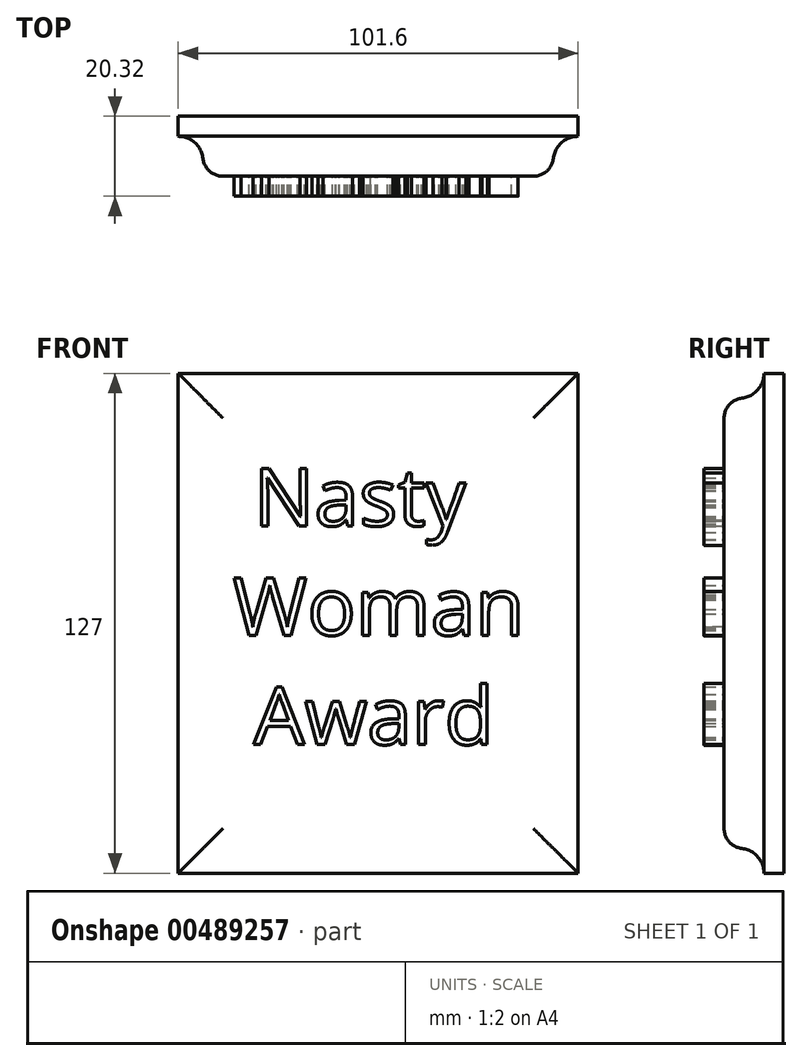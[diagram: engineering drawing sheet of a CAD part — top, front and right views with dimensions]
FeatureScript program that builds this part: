
annotation { "Feature Type Name" : "Feature", "Feature Type Description" : "" }
export const myFeature = defineFeature(function(context is Context, id is Id, definition is map)
    precondition{}
    {
        {
            var Q0;
            Q0=qCreatedBy(makeId("Front.planeOp"),FACE);
            var sketch = newSketch(context, id + "F0", { "sketchPlane" : qUnion([Q0])});
            skLineSegment(sketch, "E0.bottom", {"start": v(-101.6, 127) * mm, "end": v(0, 127) * mm});
            skLineSegment(sketch, "E0.top", {"start": v(-101.6, 0) * mm, "end": v(0, 0) * mm});
            skLineSegment(sketch, "E0.left", {"start": v(-101.6, 127) * mm, "end": v(-101.6, 0) * mm});
            skLineSegment(sketch, "E0.right", {"start": v(0, 127) * mm, "end": v(0, 0) * mm});
            skSolve(sketch);
        }
        {
            var Q0;
            Q0 = qSketchRegion(id + "F0", true);
            extrude(context, id + "F1", {"entities" : qUnion([Q0]), "depth" : 15.24 * mm});
        }
        {
            var Q0;
            Q0=makeQuery(id+"F1.opExtrude","CAP_FACE",FACE,{"disambiguationData":[OSD([sQuery(id+"F0.wireOp",EDGE,"E0.bottom"),sQuery(id+"F0.wireOp",EDGE,"E0.top"),sQuery(id+"F0.wireOp",EDGE,"E0.left"),sQuery(id+"F0.wireOp",EDGE,"E0.right")])],"isStart":false});
            var sketch = newSketch(context, id + "F2", { "sketchPlane" : qUnion([Q0])});
            skLineSegment(sketch, "E1.bottom", {"start": v(-6.35, 6.35) * mm, "end": v(-95.25, 6.35) * mm});
            skLineSegment(sketch, "E1.top", {"start": v(-6.35, 120.65) * mm, "end": v(-95.25, 120.65) * mm});
            skLineSegment(sketch, "E1.left", {"start": v(-6.35, 6.35) * mm, "end": v(-6.35, 120.65) * mm});
            skLineSegment(sketch, "E1.right", {"start": v(-95.25, 6.35) * mm, "end": v(-95.25, 120.65) * mm});
            skLineSegment(sketch, "E2.bottom", {"start": v(-101.6, 127) * mm, "end": v(0, 127) * mm});
            skLineSegment(sketch, "E2.top", {"start": v(-101.6, 0) * mm, "end": v(0, 0) * mm});
            skLineSegment(sketch, "E2.left", {"start": v(-101.6, 127) * mm, "end": v(-101.6, 0) * mm});
            skLineSegment(sketch, "E2.right", {"start": v(0, 127) * mm, "end": v(0, 0) * mm});
            skSolve(sketch);
        }
        {
            var Q0;
            Q0 = qSketchRegion(id + "F2", true);
            extrude(context, id + "F3", {"entities" : qUnion([Q0]), "operationType" : NewBodyOperationType.REMOVE, "oppositeDirection" : true, "depth" : 10.16 * mm});
        }
        {
            var Q0;
            Q0=makeQuery(id+"F3.boolean.opBoolean","COPY",EDGE,{"derivedFrom":makeQuery(id+"F3.opExtrude","CAP_EDGE",EDGE,{"disambiguationData":[OSD([sQuery(id+"F2.wireOp",EDGE,"E1.top")])],"isStart":false})});
            var Q1;
            Q1=makeQuery(id+"F3.boolean.opBoolean","COPY",EDGE,{"derivedFrom":makeQuery(id+"F3.opExtrude","CAP_EDGE",EDGE,{"disambiguationData":[OSD([sQuery(id+"F2.wireOp",EDGE,"E1.left")])],"isStart":false})});
            var Q2;
            Q2=makeQuery(id+"F3.boolean.opBoolean","COPY",EDGE,{"derivedFrom":makeQuery(id+"F3.opExtrude","CAP_EDGE",EDGE,{"disambiguationData":[OSD([sQuery(id+"F2.wireOp",EDGE,"E1.right")])],"isStart":false})});
            var Q3;
            Q3=makeQuery(id+"F3.boolean.opBoolean","COPY",EDGE,{"derivedFrom":makeQuery(id+"F3.opExtrude","CAP_EDGE",EDGE,{"disambiguationData":[OSD([sQuery(id+"F2.wireOp",EDGE,"E1.bottom")])],"isStart":false})});
            fillet(context, id + "F4", {"entities" : qUnion([Q0, Q1, Q2, Q3]), "radius" : 6.35 * mm, "tangentPropagation" : true, "allowEdgeOverflow" : false});
        }
        {
            var Q0;
            Q0=makeQuery(id+"F1.opExtrude","CAP_FACE",FACE,{"disambiguationData":[OSD([sQuery(id+"F0.wireOp",EDGE,"E0.bottom"),sQuery(id+"F0.wireOp",EDGE,"E0.top"),sQuery(id+"F0.wireOp",EDGE,"E0.left"),sQuery(id+"F0.wireOp",EDGE,"E0.right")])],"isStart":false});
            fillet(context, id + "F5", {"entities" : qUnion([Q0]), "radius" : 5.08 * mm, "tangentPropagation" : true, "allowEdgeOverflow" : false});
        }
        {
            var Q0;
            Q0=makeQuery(id+"F1.opExtrude","CAP_FACE",FACE,{"disambiguationData":[OSD([sQuery(id+"F0.wireOp",EDGE,"E0.bottom"),sQuery(id+"F0.wireOp",EDGE,"E0.top"),sQuery(id+"F0.wireOp",EDGE,"E0.left"),sQuery(id+"F0.wireOp",EDGE,"E0.right")])],"isStart":false});
            var sketch = newSketch(context, id + "F6", { "sketchPlane" : qUnion([Q0])});
            skText(sketch, "E3", { "text": " Nasty\nWoman\n Award", "fontName": "OpenSans-Regular.ttf"});
            const initialGuessF6  = {"E3": [-0.0877, 0.08824, 1, 0, 0.0147]};
            skSetInitialGuess(sketch, initialGuessF6);
            skSolve(sketch);
        }
        {
            var Q0;
            Q0 = qSketchRegion(id + "F6", true);
            extrude(context, id + "F7", {"entities" : qUnion([Q0]), "operationType" : NewBodyOperationType.ADD, "depth" : 5.08 * mm});
        }
    });
